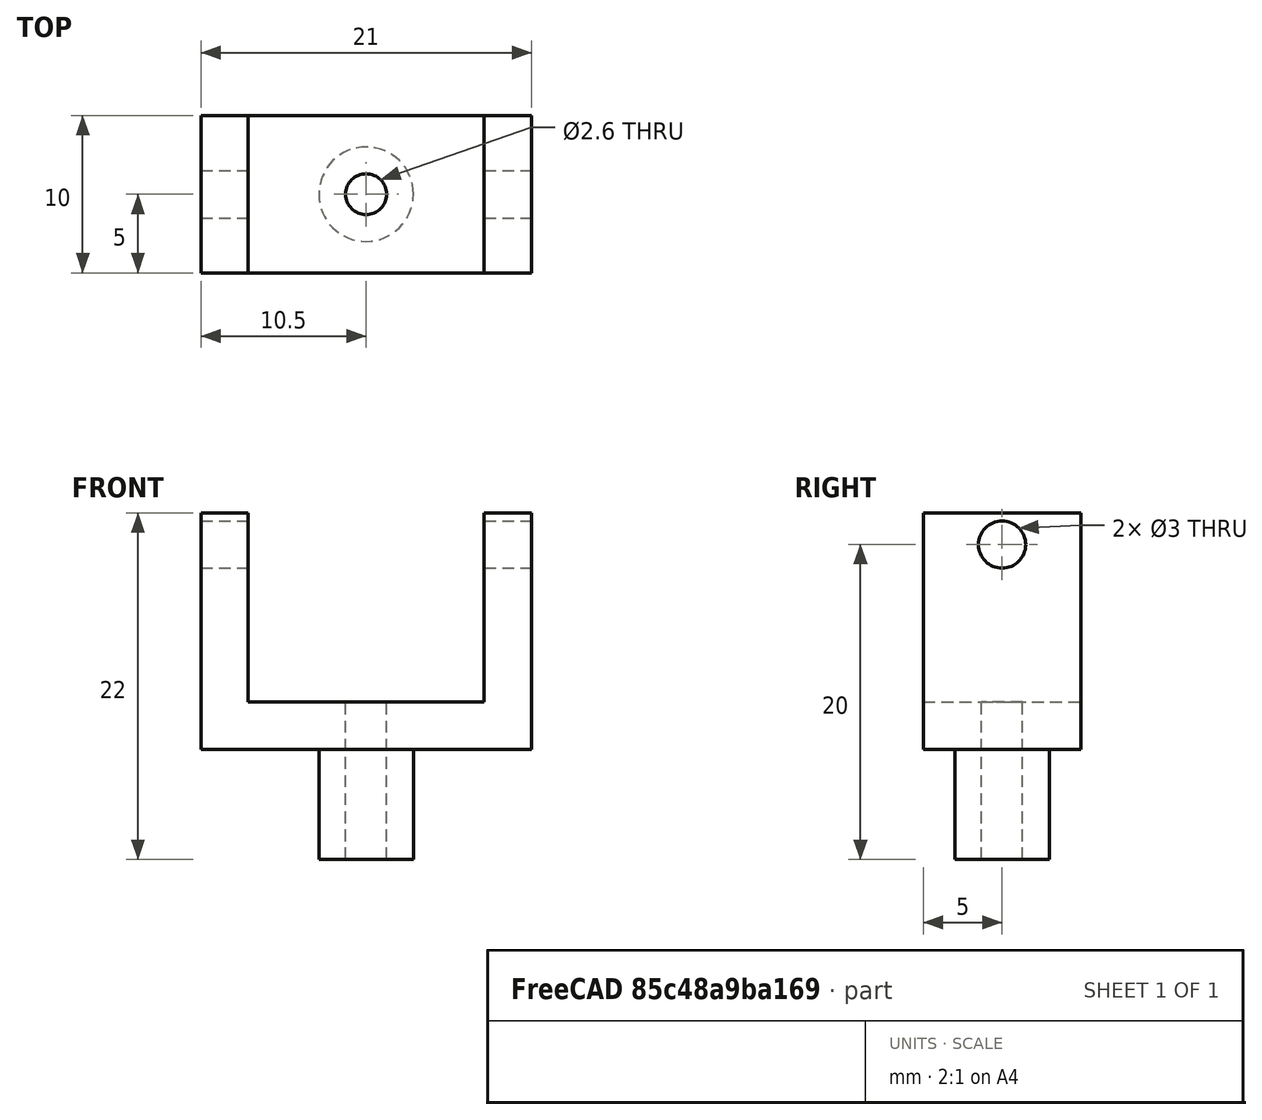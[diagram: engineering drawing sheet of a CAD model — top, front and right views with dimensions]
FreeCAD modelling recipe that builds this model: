
FCSTD DOCUMENT  (FreeCAD 0.14R3702 (Git))
Label: support
License: CC-BY 3.0
LicenseURL: http://creativecommons.org/licenses/by/3.0/
objects: Part::Cylinder×4, Part::Box×3, Part::Cut×3, Part::MultiFuse×2
note: 12 computed .brp shape members not serialized (recipe doc carries the construction recipe); baked Part::Feature solids carry a one-line shape summary decoded from their .brp

FEATURE [Part::Box] Box  label="Cube"
  Height = 3
  Length = 21
  Width = 10
FEATURE [Part::Box] Box001  label="Cube001"
  Height = 15
  Length = 3
  Width = 10
FEATURE [Part::Box] Box002  label="Cube002"
  Height = 15
  Length = 3
  Placement = pos=(18,0,0) rot=(0,0,1;0rad)
  Width = 10
FEATURE [Part::Cylinder] Cylinder  label="Hole1"
  Angle = 360
  Height = 3
  Placement = pos=(0,5,13) rot=(0,1,0;1.5708rad)
  Radius = 1.5
FEATURE [Part::Cylinder] Cylinder001  label="Hole002"
  Angle = 360
  Height = 3
  Placement = pos=(18,5,13) rot=(0,1,0;1.5708rad)
  Radius = 1.5
FEATURE [Part::Cylinder] Cylinder002  label="Cylinder"
  Angle = 360
  Height = 8
  Placement = pos=(10.5,5,-7) rot=(0,0,1;0rad)
  Radius = 3
FEATURE [Part::Cylinder] Cylinder003  label="Cylinder001"
  Angle = 360
  Height = 10
  Placement = pos=(10.5,5,-7) rot=(0,0,1;0rad)
  Radius = 1.3
FEATURE [Part::MultiFuse] Fusion
  Shapes = -> [Box,Box001,Box002]
FEATURE [Part::MultiFuse] Fusion001
  Shapes = -> [Fusion,Cylinder002]
FEATURE [Part::Cut] Cut
  Base = -> Fusion001
  Tool = -> Cylinder
FEATURE [Part::Cut] Cut001
  Base = -> Cut
  Tool = -> Cylinder001
FEATURE [Part::Cut] Cut002
  Base = -> Cut001
  Tool = -> Cylinder003
